# Revit family: 18. Вертикальная заслонка ANR K1
name_source: partatom
category: Оборудование
revit_build: Autodesk Revit 2016 (Build: 20161004_0715(x64)
units: mm (PartAtom-declared; Revit-internal decimal feet)

## family parameters
Всегда вертикально = Да
На основе рабочей плоскости = Нет
Общий = Нет
При загрузке вырезать с полостями = Нет
Размер круглого соединителя = Использовать диаметр
Тип детали = Нормальный
Точка расчета площади = Нет

## types (10) — shared parameters
Д = 125 мм
Единица измерения = шт.
Завод изготовитель = KORF
Ключевая пометка = Вентиляция
Материал = Сталь серая
Наименование и тех.хар-ка = Вертикальная заслонка
Раздел = ОВ

## per-type parameters (varying)
| type | d | А | А1 | А2 | Б | Б1 | Б2 | Высота | Середина | Ширина | Ширина лопатки | пл | р | №12 | №20 | №25 | №30 | №35 | №40 | №45 | №6 | №7 | №8 |
| ANR 6 K1 | 16 мм | 1040 мм | 1020 мм | 980 мм | 540 мм | 510 мм | 480 мм | 4015 мм | 270 мм | 1550 мм | 53 мм | 54 мм | 26 мм | Нет | Нет | Нет | Нет | Нет | Нет | Нет | Да | Нет | Нет |
| ANR 7 K1 | 16 мм | 1040 мм | 1020 мм | 980 мм | 740 мм | 710 мм | 680 мм | 1245 мм | 370 мм | 1025 мм | 53 мм | 74 мм | 26 мм | Нет | Нет | Нет | Нет | Нет | Нет | Нет | Нет | Да | Нет |
| ANR 8 K1 | 19 мм | 1240 мм | 1220 мм | 1180 мм | 740 мм | 710 мм | 680 мм | 1245 мм | 370 мм | 1550 мм | 63 мм | 74 мм | 31 мм | Нет | Нет | Нет | Нет | Нет | Нет | Нет | Нет | Нет | Да |
| ANR 12 K1 | 21 мм | 1358 мм | 1338 мм | 1298 мм | 840 мм | 810 мм | 780 мм | 1360 мм | 420 мм | 1550 мм | 69 мм | 84 мм | 34 мм | Да | Нет | Нет | Нет | Нет | Нет | Нет | Нет | Нет | Нет |
| ANR 20 K1 | 24 мм | 1582 мм | 1562 мм | 1522 мм | 1040 мм | 1010 мм | 980 мм | 1585 мм | 520 мм | 1550 мм | 81 мм | 104 мм | 40 мм | Нет | Да | Нет | Нет | Нет | Нет | Нет | Нет | Нет | Нет |
| ANR 25 K1 | 30 мм | 1968 мм | 1948 мм | 1908 мм | 1440 мм | 1410 мм | 1380 мм | 1970 мм | 720 мм | 1550 мм | 100 мм | 144 мм | 49 мм | Нет | Нет | Да | Нет | Нет | Нет | Нет | Нет | Нет | Нет |
| ANR 30 K1 | 37 мм | 2408 мм | 2388 мм | 2348 мм | 1440 мм | 1410 мм | 1380 мм | 1970 мм | 720 мм | 2075 мм | 123 мм | 144 мм | 60 мм | Нет | Нет | Нет | Да | Нет | Нет | Нет | Нет | Нет | Нет |
| ANR 35 K1 | 37 мм | 2408 мм | 2388 мм | 2348 мм | 1940 мм | 1910 мм | 1880 мм | 2410 мм | 970 мм | 2075 мм | 123 мм | 194 мм | 60 мм | Нет | Нет | Нет | Нет | Да | Нет | Нет | Нет | Нет | Нет |
| ANR 40 K1 | 51 мм | 3292 мм | 3231 мм | 3232 мм | 2120 мм | 2071 мм | 2060 мм | 3245 мм | 1060 мм | 1550 мм | 168 мм | 212 мм | 82 мм | Нет | Нет | Нет | Нет | Нет | Да | Нет | Нет | Нет | Нет |
| ANR 45 K1 | 51 мм | 3292 мм | 3231 мм | 3232 мм | 2120 мм | 2071 мм | 2060 мм | 4015 мм | 1060 мм | 1550 мм | 168 мм | 212 мм | 82 мм | Нет | Нет | Нет | Нет | Нет | Нет | Да | Нет | Нет | Нет |

note: column(s) folded — value = type name in every type: Тип, марка, обозначение
